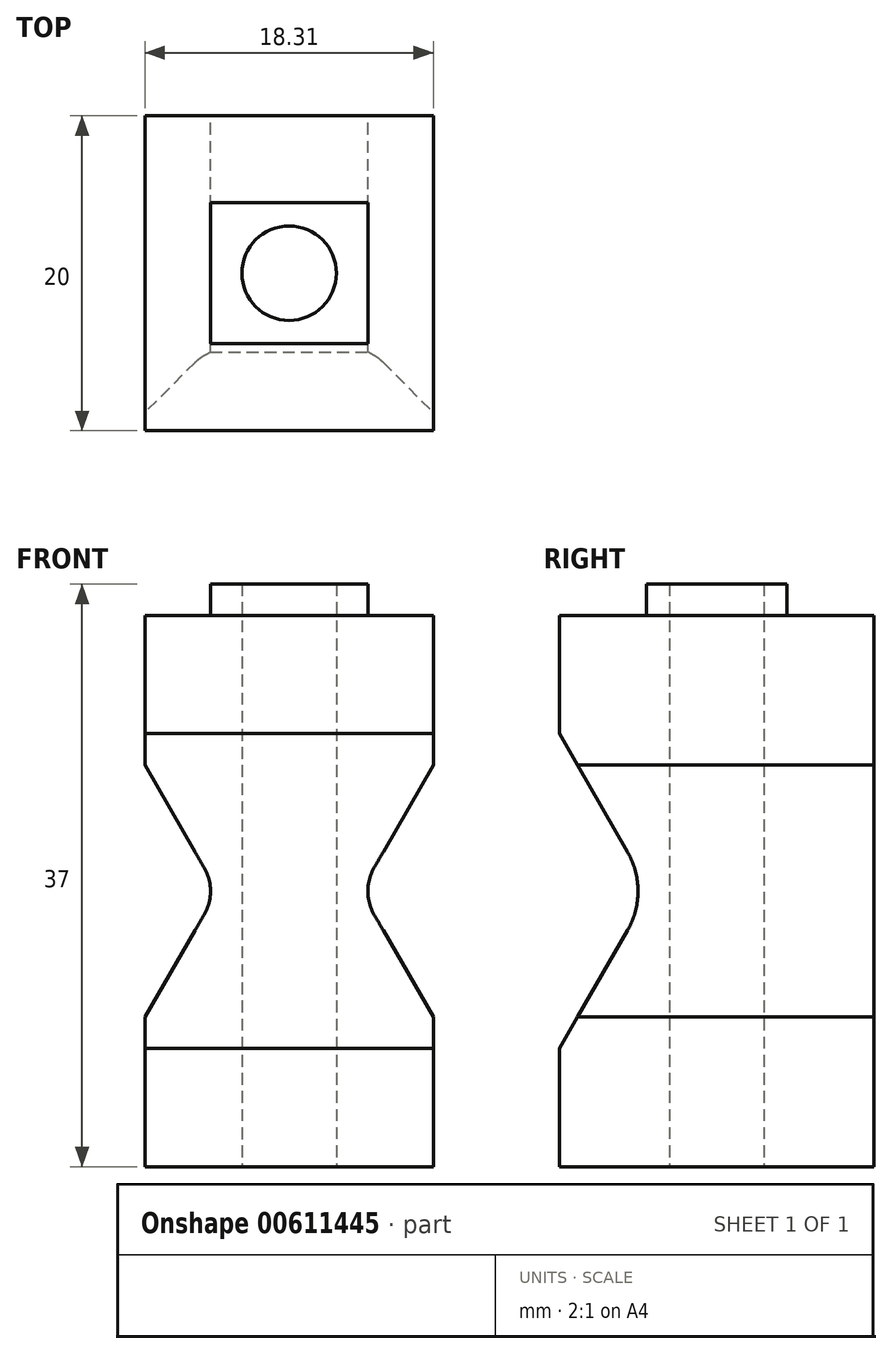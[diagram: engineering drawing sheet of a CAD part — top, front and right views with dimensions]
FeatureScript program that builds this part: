
annotation { "Feature Type Name" : "Feature", "Feature Type Description" : "" }
export const myFeature = defineFeature(function(context is Context, id is Id, definition is map)
    precondition{}
    {
        {
            var Q0;
            Q0=qCreatedBy(makeId("Front.planeOp"),FACE);
            var sketch = newSketch(context, id + "F0", { "sketchPlane" : qUnion([Q0])});
            skPoint(sketch, "E0.0", {"position": v(0, 0) * mm});
            skCircle(sketch, "E1", {"center": v(0, 0) * mm, "radius": 4 * mm});
            skLineSegment(sketch, "E2", {"start": v(-4.62, 0) * mm, "end": v(0, 8) * mm});
            skLineSegment(sketch, "E3", {"start": v(0, 8) * mm, "end": v(-3.75, 1.5) * mm});
            skLineSegment(sketch, "E4", {"start": v(-3.75, -1.5) * mm, "end": v(0, -8) * mm});
            skCircle(sketch, "E5", {"center": v(13.86, 0) * mm, "radius": 16 * mm});
            skLineSegment(sketch, "E6", {"start": v(0, 8) * mm, "end": v(0, 17.5) * mm});
            skLineSegment(sketch, "E7", {"start": v(0, 17.5) * mm, "end": v(-18.3, 17.5) * mm});
            skLineSegment(sketch, "E8", {"start": v(-18.3, 17.5) * mm, "end": v(-18.3, 8) * mm});
            skLineSegment(sketch, "E9", {"start": v(-18.3, -17.5) * mm, "end": v(0, -17.5) * mm});
            skLineSegment(sketch, "E10", {"start": v(0, -17.5) * mm, "end": v(0, -8) * mm});
            skLineSegment(sketch, "E11", {"start": v(-18.3, 8) * mm, "end": v(-14.56, 1.5) * mm});
            skLineSegment(sketch, "E12", {"start": v(-14.56, -1.5) * mm, "end": v(-18.3, -8) * mm});
            skLineSegment(sketch, "E13.trimOffspring", {"start": v(-18.3, -8) * mm, "end": v(-18.3, -17.5) * mm});
            skPoint(sketch, "E14.visualSharp", {"position": v(-4.62, 0) * mm});
            skArc(sketch, "E14.filletArc", {"start": v(-3.75, 1.5) * mm, "mid": v(-4.15, 0) * mm, "end": v(-3.75, -1.5) * mm});
            skPoint(sketch, "E15.visualSharp", {"position": v(-13.7, 0) * mm});
            skArc(sketch, "E15.filletArc", {"start": v(-14.56, -1.5) * mm, "mid": v(-14.15, 0) * mm, "end": v(-14.56, 1.5) * mm});
            skSolve(sketch);
        }
        {
            var Q0;
            {var subQ0=sQuery(id+"F0.wireOp",EDGE,"E6");Q0=makeQuery(id+"F0.imprint","IMPRINT",FACE,{"disambiguationData":[TD([[makeQuery(id+"F0.imprint","IMPRINT",EDGE,{"derivedFrom":subQ0}),1.0]])]});}
            var Q1;
            Q1=sQuery(id+"F0.wireOp",EDGE,"E7");
            var Q2;
            Q2=sQuery(id+"F0.wireOp",EDGE,"E6");
            var Q3;
            Q3=sQuery(id+"F0.wireOp",EDGE,"E3");
            var Q4;
            Q4=sQuery(id+"F0.wireOp",EDGE,"E4");
            var Q5;
            Q5=sQuery(id+"F0.wireOp",EDGE,"E12");
            var Q6;
            Q6=sQuery(id+"F0.wireOp",EDGE,"E13.trimOffspring");
            var Q7;
            Q7=sQuery(id+"F0.wireOp",EDGE,"E9");
            var Q8;
            Q8=sQuery(id+"F0.wireOp",EDGE,"E10");
            var Q9;
            Q9=sQuery(id+"F0.wireOp",EDGE,"E8");
            var Q10;
            Q10=sQuery(id+"F0.wireOp",EDGE,"E11");
            extrude(context, id + "F1", {"entities" : qUnion([Q0]), "surfaceEntities" : qUnion([Q1, Q2, Q3, Q4, Q5, Q6, Q7, Q8, Q9, Q10]), "endBound" : BoundingType.SYMMETRIC, "depth" : 20 * mm, "offsetDistance" : 25 * mm});
        }
        {
            var Q0;
            Q0=qCreatedBy(makeId("Right.planeOp"),FACE);
            var sketch = newSketch(context, id + "F2", { "sketchPlane" : qUnion([Q0])});
            skLineSegment(sketch, "E16.0", {"start": v(-10, 17.5) * mm, "end": v(10, 17.5) * mm});
            skLineSegment(sketch, "E17.0", {"start": v(-10, 8) * mm, "end": v(10, 8) * mm});
            skLineSegment(sketch, "E18.0", {"start": v(-10, -17.5) * mm, "end": v(10, -17.5) * mm});
            skLineSegment(sketch, "E19.0", {"start": v(-10, 8) * mm, "end": v(-10, 17.5) * mm});
            skLineSegment(sketch, "E20.0", {"start": v(-10, 8) * mm, "end": v(-10, 1.5) * mm});
            skLineSegment(sketch, "E21.0", {"start": v(-10, 1.5) * mm, "end": v(-10, -8) * mm});
            skLineSegment(sketch, "E22.0", {"start": v(-10, -17.5) * mm, "end": v(-10, -8) * mm});
            skLineSegment(sketch, "E23.0", {"start": v(10, -17.5) * mm, "end": v(10, -8) * mm});
            skLineSegment(sketch, "E24.0", {"start": v(10, -1.5) * mm, "end": v(10, -8) * mm});
            skPoint(sketch, "E25.0", {"position": v(10, 4.75) * mm});
            skLineSegment(sketch, "E26.0", {"start": v(10, 8) * mm, "end": v(10, -1.5) * mm});
            skLineSegment(sketch, "E27.0", {"start": v(10, 8) * mm, "end": v(10, 17.5) * mm});
            skLineSegment(sketch, "E28", {"start": v(-10, 10) * mm, "end": v(-5.67, 2.5) * mm});
            skLineSegment(sketch, "E29", {"start": v(-5.67, -2.5) * mm, "end": v(-10, -10) * mm});
            skCircle(sketch, "E30", {"center": v(-22.7, 0) * mm, "radius": 16 * mm});
            skPoint(sketch, "E31.visualSharp", {"position": v(-4.23, 0) * mm});
            skArc(sketch, "E31.filletArc", {"start": v(-5.67, -2.5) * mm, "mid": v(-5, 0) * mm, "end": v(-5.67, 2.5) * mm});
            skSolve(sketch);
        }
        {
            var Q0;
            {var subQ1=sQuery(id+"F2.wireOp",EDGE,"E20.0");Q0=makeQuery(id+"F2.imprint","IMPRINT",FACE,{"disambiguationData":[TD([[makeQuery(id+"F2.imprint","IMPRINT",EDGE,{"derivedFrom":subQ1}),1.0]])]});}
            var Q1;
            {var subQ0=sQuery(id+"F2.wireOp",EDGE,"E19.0");var subQ3=sQuery(id+"F2.wireOp",EDGE,"E30");var subQ5=makeQuery(id+"F2.imprint","INTERSECT",VERTEX,{"derivedFrom":[subQ0,subQ3]});Q1=makeQuery(id+"F2.imprint","IMPRINT",FACE,{"disambiguationData":[TD([[makeQuery(id+"F2.imprint","IMPRINT",EDGE,{"disambiguationData":[TD([[subQ5,1.0]])],"derivedFrom":subQ0}),-1.0]])]});}
            var Q2;
            {var subQ0=sQuery(id+"F2.wireOp",EDGE,"E31.filletArc");Q2=makeQuery(id+"F2.imprint","IMPRINT",FACE,{"disambiguationData":[TD([[makeQuery(id+"F2.imprint","IMPRINT",EDGE,{"derivedFrom":subQ0}),1.0]])]});}
            var Q3;
            {var subQ0=sQuery(id+"F2.wireOp",EDGE,"E28");var subQ1=sQuery(id+"F2.wireOp",EDGE,"E19.0");var subQ2=makeQuery(id+"F2.imprint","INTERSECT",VERTEX,{"derivedFrom":[subQ1,subQ0]});Q3=makeQuery(id+"F2.imprint","IMPRINT",FACE,{"disambiguationData":[TD([[makeQuery(id+"F2.imprint","IMPRINT",EDGE,{"disambiguationData":[TD([[subQ2,1.0]])],"derivedFrom":subQ1}),-1.0]])]});}
            var Q4;
            {var subQ0=sQuery(id+"F2.wireOp",EDGE,"E29");var subQ1=sQuery(id+"F2.wireOp",EDGE,"E22.0");var subQ2=makeQuery(id+"F2.imprint","INTERSECT",VERTEX,{"derivedFrom":[subQ1,subQ0]});Q4=makeQuery(id+"F2.imprint","IMPRINT",FACE,{"disambiguationData":[TD([[makeQuery(id+"F2.imprint","IMPRINT",EDGE,{"disambiguationData":[TD([[subQ2,-1.0]])],"derivedFrom":subQ1}),-1.0]])]});}
            extrude(context, id + "F3", {"entities" : qUnion([Q0, Q1, Q2, Q3, Q4]), "operationType" : NewBodyOperationType.REMOVE, "endBound" : BoundingType.THROUGH_ALL, "oppositeDirection" : true, "depth" : 25 * mm, "offsetDistance" : 25 * mm});
        }
        {
            var Q0;
            Q0=makeQuery(id+"F1.opExtrude","SWEPT_FACE",FACE,{"disambiguationData":[OSD([sQuery(id+"F0.wireOp",EDGE,"E9")])]});
            var sketch = newSketch(context, id + "F4", { "sketchPlane" : qUnion([Q0])});
            skLineSegment(sketch, "E32.0.0", {"start": v(-18.3, -10) * mm, "end": v(0, -10) * mm});
            skLineSegment(sketch, "E32.0.1", {"start": v(0, -10) * mm, "end": v(0, 10) * mm});
            skLineSegment(sketch, "E32.0.2", {"start": v(0, 10) * mm, "end": v(-18.3, 10) * mm});
            skLineSegment(sketch, "E32.0.3", {"start": v(-18.3, 10) * mm, "end": v(-18.3, -10) * mm});
            skLineSegment(sketch, "E33", {"start": v(0, -10) * mm, "end": v(-18.3, 10) * mm});
            skCircle(sketch, "E34", {"center": v(-9.15, 0) * mm, "radius": 3 * mm});
            skSolve(sketch);
        }
        {
            var Q0;
            {var subQ0=sQuery(id+"F4.wireOp",EDGE,"E34");var subQ1=sQuery(id+"F4.wireOp",EDGE,"E33");var subQ2=makeQuery(id+"F4.imprint","INTERSECT",VERTEX,{"disambiguationData":[OD(0.0)],"derivedFrom":[subQ1,subQ0]});Q0=makeQuery(id+"F4.imprint","IMPRINT",FACE,{"disambiguationData":[TD([[makeQuery(id+"F4.imprint","IMPRINT",EDGE,{"disambiguationData":[TD([[subQ2,-1.0]])],"derivedFrom":subQ1}),-1.0]])]});}
            var Q1;
            {var subQ0=sQuery(id+"F4.wireOp",EDGE,"E34");var subQ1=sQuery(id+"F4.wireOp",EDGE,"E33");var subQ2=makeQuery(id+"F4.imprint","INTERSECT",VERTEX,{"disambiguationData":[OD(0.0)],"derivedFrom":[subQ1,subQ0]});Q1=makeQuery(id+"F4.imprint","IMPRINT",FACE,{"disambiguationData":[TD([[makeQuery(id+"F4.imprint","IMPRINT",EDGE,{"disambiguationData":[TD([[subQ2,-1.0]])],"derivedFrom":subQ1}),1.0]])]});}
            extrude(context, id + "F5", {"entities" : qUnion([Q0, Q1]), "operationType" : NewBodyOperationType.REMOVE, "endBound" : BoundingType.THROUGH_ALL, "oppositeDirection" : true, "depth" : 25 * mm, "offsetDistance" : 25 * mm});
        }
        {
            var Q0;
            Q0=makeQuery(id+"F1.opExtrude","SWEPT_FACE",FACE,{"disambiguationData":[OSD([sQuery(id+"F0.wireOp",EDGE,"E7")])]});
            var sketch = newSketch(context, id + "F6", { "sketchPlane" : qUnion([Q0])});
            skLineSegment(sketch, "E35.bottom", {"start": v(-14.15, 4.47) * mm, "end": v(-4.15, 4.47) * mm});
            skLineSegment(sketch, "E35.top", {"start": v(-14.15, -4.47) * mm, "end": v(-4.15, -4.47) * mm});
            skLineSegment(sketch, "E35.left", {"start": v(-14.15, 4.47) * mm, "end": v(-14.15, -4.47) * mm});
            skLineSegment(sketch, "E35.right", {"start": v(-4.15, 4.47) * mm, "end": v(-4.15, -4.47) * mm});
            skPoint(sketch, "E35.middle", {"position": v(-9.15, 0) * mm});
            skSolve(sketch);
        }
        {
            var Q0;
            Q0=makeQuery(id+"F6.imprint","IMPRINT",FACE,{"disambiguationData":[TD([[makeQuery(id+"F6.imprint","IMPRINT",EDGE,{"derivedFrom":sQuery(id+"F6.wireOp",EDGE,"E35.bottom")}),-1.0]])]});
            extrude(context, id + "F7", {"entities" : qUnion([Q0]), "operationType" : NewBodyOperationType.ADD, "depth" : 2 * mm, "offsetDistance" : 25 * mm});
        }
    });
